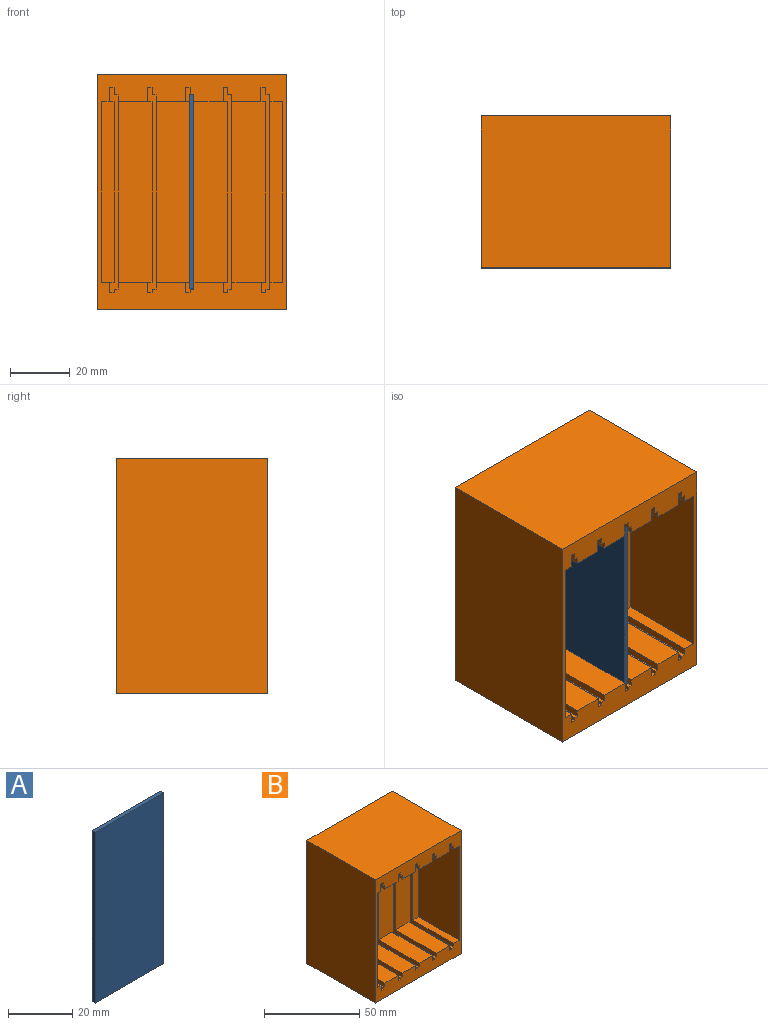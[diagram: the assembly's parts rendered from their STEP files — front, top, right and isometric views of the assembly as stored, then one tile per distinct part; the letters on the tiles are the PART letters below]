
ASSEMBLY  parts=2 mates=1
PART A: 6 faces, bbox 30.1x1.3x65 mm
  f0: plane 64.99x1.33mm, normal (1,0,0), area 86.7mm2, adj f1,f3,f4,f5
  f1: plane 30.14x1.33mm, normal (0,0,1), area 40.2mm2, adj f0,f2,f4,f5
  f2: plane 64.99x1.33mm, normal (-1,0,0), area 86.7mm2, adj f1,f3,f4,f5
  f3: plane 30.14x1.33mm, normal (0,0,-1), area 40.2mm2, adj f0,f2,f4,f5
  f4: plane 64.99x30.14mm, normal (0,-1,0), area 1958.5mm2, adj f0,f1,f2,f3
  f5: plane 64.99x30.14mm, normal (0,1,0), area 1958.5mm2, adj f0,f1,f2,f3
PART B: 91 faces, bbox 63.5x50.8x79 mm
  f0: plane 30.14x2.64mm, normal (0,0,-1), area 79.6mm2, adj f37,f38,f63,f85
  f1: plane 30.14x9.72mm, normal (0,0,-1), area 292.8mm2, adj f31,f42,f63,f81
  f2: plane 30.14x9.72mm, normal (0,0,-1), area 292.8mm2, adj f25,f46,f63,f77
  f3: plane 30.14x9.72mm, normal (0,0,-1), area 292.8mm2, adj f19,f50,f63,f73
  f4: plane 30.14x9.72mm, normal (0,0,-1), area 292.8mm2, adj f13,f54,f63,f69
  f5: plane 60.39x30.14mm, normal (-1,0,0), area 1819.9mm2, adj f6,f62,f63,f65
  f6: plane 30.14x4.29mm, normal (0,0,1), area 129.4mm2, adj f5,f7,f63,f65
  f7: plane 64.99x32.44mm, normal (-1,0,0), area 287.9mm2, adj f6,f8,f57,f62,f63,f65,f86
  f8: plane 32.44x1.33mm, normal (0,0,1), area 43.3mm2, adj f7,f9,f63,f86
  f9: plane 32.44x1.05mm, normal (-1,0,0), area 34.2mm2, adj f8,f10,f63,f86
  f10: plane 32.44x1.45mm, normal (0,0,1), area 47mm2, adj f9,f11,f63,f86
  f11: plane 32.44x3.35mm, normal (1,0,0), area 108.8mm2, adj f10,f12,f63,f66,f86
  f12: plane 30.14x9.92mm, normal (0,0,1), area 298.9mm2, adj f11,f13,f63,f69
  f13: plane 64.99x32.44mm, normal (-1,0,0), area 287.9mm2, adj f4,f12,f14,f53,f63,f69,f87
  f14: plane 32.44x1.33mm, normal (0,0,1), area 43.3mm2, adj f13,f15,f63,f87
  f15: plane 32.44x1.05mm, normal (-1,0,0), area 34.2mm2, adj f14,f16,f63,f87
  f16: plane 32.44x1.45mm, normal (0,0,1), area 47mm2, adj f15,f17,f63,f87
  f17: plane 32.44x3.35mm, normal (1,0,0), area 108.8mm2, adj f16,f18,f63,f70,f87
  f18: plane 30.14x9.92mm, normal (0,0,1), area 298.9mm2, adj f17,f19,f63,f73
  f19: plane 64.99x32.44mm, normal (-1,0,0), area 287.9mm2, adj f3,f18,f20,f49,f63,f73,f88
  f20: plane 32.44x1.33mm, normal (0,0,1), area 43.3mm2, adj f19,f21,f63,f88
  f21: plane 32.44x1.05mm, normal (-1,0,0), area 34.2mm2, adj f20,f22,f63,f88
  f22: plane 32.44x1.45mm, normal (0,0,1), area 47mm2, adj f21,f23,f63,f88
  f23: plane 32.44x3.35mm, normal (1,0,0), area 108.8mm2, adj f22,f24,f63,f74,f88
  f24: plane 30.14x9.92mm, normal (0,0,1), area 298.9mm2, adj f23,f25,f63,f77
  f25: plane 64.99x32.44mm, normal (-1,0,0), area 287.9mm2, adj f2,f24,f26,f45,f63,f77,f89
  f26: plane 32.44x1.33mm, normal (0,0,1), area 43.3mm2, adj f25,f27,f63,f89
  f27: plane 32.44x1.05mm, normal (-1,0,0), area 34.2mm2, adj f26,f28,f63,f89
  f28: plane 32.44x1.45mm, normal (0,0,1), area 47mm2, adj f27,f29,f63,f89
  f29: plane 32.44x3.35mm, normal (1,0,0), area 108.8mm2, adj f28,f30,f63,f78,f89
  f30: plane 30.14x9.92mm, normal (0,0,1), area 298.9mm2, adj f29,f31,f63,f81
  f31: plane 64.99x32.44mm, normal (-1,0,0), area 287.9mm2, adj f1,f30,f32,f41,f63,f81,f90
  f32: plane 32.44x1.33mm, normal (0,0,1), area 43.3mm2, adj f31,f33,f63,f90
  f33: plane 32.44x1.05mm, normal (-1,0,0), area 34.2mm2, adj f32,f34,f63,f90
  f34: plane 32.44x1.45mm, normal (0,0,1), area 47mm2, adj f33,f35,f63,f90
  f35: plane 32.44x3.35mm, normal (1,0,0), area 108.8mm2, adj f34,f36,f63,f82,f90
  f36: plane 30.14x2.85mm, normal (0,0,1), area 85.7mm2, adj f35,f37,f63,f85
  f37: plane 60.39x30.14mm, normal (1,0,0), area 1819.9mm2, adj f0,f36,f63,f85
  f38: plane 32.44x4.71mm, normal (1,0,0), area 152.8mm2, adj f0,f39,f63,f84,f90
  f39: plane 32.44x1.65mm, normal (0,0,-1), area 53.6mm2, adj f38,f40,f63,f90
  f40: plane 32.44x2.41mm, normal (-1,0,0), area 78.3mm2, adj f39,f41,f63,f90
  f41: plane 32.44x1.33mm, normal (0,0,-1), area 43.3mm2, adj f31,f40,f63,f90
  f42: plane 32.44x4.71mm, normal (1,0,0), area 152.8mm2, adj f1,f43,f63,f80,f89
  f43: plane 32.44x1.65mm, normal (0,0,-1), area 53.6mm2, adj f42,f44,f63,f89
  f44: plane 32.44x2.41mm, normal (-1,0,0), area 78.3mm2, adj f43,f45,f63,f89
  f45: plane 32.44x1.33mm, normal (0,0,-1), area 43.3mm2, adj f25,f44,f63,f89
  f46: plane 32.44x4.71mm, normal (1,0,0), area 152.8mm2, adj f2,f47,f63,f76,f88
  f47: plane 32.44x1.65mm, normal (0,0,-1), area 53.6mm2, adj f46,f48,f63,f88
  f48: plane 32.44x2.41mm, normal (-1,0,0), area 78.3mm2, adj f47,f49,f63,f88
  f49: plane 32.44x1.33mm, normal (0,0,-1), area 43.3mm2, adj f19,f48,f63,f88
  f50: plane 32.44x4.71mm, normal (1,0,0), area 152.8mm2, adj f3,f51,f63,f72,f87
  f51: plane 32.44x1.61mm, normal (0,0,-1), area 52.3mm2, adj f50,f52,f63,f87
  f52: plane 32.44x2.41mm, normal (-1,0,0), area 78.3mm2, adj f51,f53,f63,f87
  f53: plane 32.44x1.37mm, normal (0,0,-1), area 44.5mm2, adj f13,f52,f63,f87
  f54: plane 32.44x4.71mm, normal (1,0,0), area 152.8mm2, adj f4,f55,f63,f68,f86
  f55: plane 32.44x1.65mm, normal (0,0,-1), area 53.6mm2, adj f54,f56,f63,f86
  f56: plane 32.44x2.41mm, normal (-1,0,0), area 78.3mm2, adj f55,f57,f63,f86
  f57: plane 32.44x1.33mm, normal (0,0,-1), area 43.3mm2, adj f7,f56,f63,f86
  f58: plane 63.5x50.8mm, normal (0,0,-1), area 3225.8mm2, adj f59,f61,f63,f64
  f59: plane 78.99x50.8mm, normal (1,0,0), area 4012.9mm2, adj f58,f60,f63,f64
  f60: plane 63.5x50.8mm, normal (0,0,1), area 3225.8mm2, adj f59,f61,f63,f64
  f61: plane 78.99x50.8mm, normal (-1,0,0), area 4012.9mm2, adj f58,f60,f63,f64
  f62: plane 30.14x4.29mm, normal (0,0,-1), area 129.4mm2, adj f5,f7,f63,f65
  f63: plane 78.99x63.5mm, normal (0,-1,0), area 1255.7mm2, adj f0,f1,f2,f3,f4,f5,f6,f7
  f64: plane 78.99x63.5mm, normal (0,1,0), area 5016.1mm2, adj f58,f59,f60,f61
  f65: plane 60.39x4.29mm, normal (0,-1,0), area 259.2mm2, adj f5,f6,f7,f62
  f66: plane 2.3x1.45mm, normal (0,0,-1), area 3.3mm2, adj f11,f67,f69,f86
  f67: plane 60.39x2.3mm, normal (1,0,0), area 138.8mm2, adj f66,f68,f69,f86
  f68: plane 2.3x1.65mm, normal (0,0,1), area 3.8mm2, adj f54,f67,f69,f86
  f69: plane 60.39x11.37mm, normal (0,-1,0), area 686.4mm2, adj f4,f12,f13,f66,f67,f68
  f70: plane 2.3x1.45mm, normal (0,0,-1), area 3.3mm2, adj f17,f71,f73,f87
  f71: plane 60.39x2.3mm, normal (1,0,0), area 138.8mm2, adj f70,f72,f73,f87
  f72: plane 2.3x1.65mm, normal (0,0,1), area 3.8mm2, adj f50,f71,f73,f87
  f73: plane 60.39x11.37mm, normal (0,-1,0), area 686.4mm2, adj f3,f18,f19,f70,f71,f72
  f74: plane 2.3x1.45mm, normal (0,0,-1), area 3.3mm2, adj f23,f75,f77,f88
  f75: plane 60.39x2.3mm, normal (1,0,0), area 138.8mm2, adj f74,f76,f77,f88
  f76: plane 2.3x1.65mm, normal (0,0,1), area 3.8mm2, adj f46,f75,f77,f88
  f77: plane 60.39x11.37mm, normal (0,-1,0), area 686.4mm2, adj f2,f24,f25,f74,f75,f76
  f78: plane 2.3x1.45mm, normal (0,0,-1), area 3.3mm2, adj f29,f79,f81,f89
  f79: plane 60.39x2.3mm, normal (1,0,0), area 138.8mm2, adj f78,f80,f81,f89
  f80: plane 2.3x1.65mm, normal (0,0,1), area 3.8mm2, adj f42,f79,f81,f89
  f81: plane 60.39x11.37mm, normal (0,-1,0), area 686.4mm2, adj f1,f30,f31,f78,f79,f80
  f82: plane 2.3x1.45mm, normal (0,0,-1), area 3.3mm2, adj f35,f83,f85,f90
  f83: plane 60.39x2.3mm, normal (1,0,0), area 138.8mm2, adj f82,f84,f85,f90
  f84: plane 2.3x1.65mm, normal (0,0,1), area 3.8mm2, adj f38,f83,f85,f90
  f85: plane 60.39x4.29mm, normal (0,-1,0), area 259.2mm2, adj f0,f36,f37,f82,f83,f84
  f86: plane 68.45x2.98mm, normal (0,-1,0), area 99.3mm2, adj f7,f8,f9,f10,f11,f54,f55,f56
  f87: plane 68.45x2.98mm, normal (0,-1,0), area 99.2mm2, adj f13,f14,f15,f16,f17,f50,f51,f52
  f88: plane 68.45x2.98mm, normal (0,-1,0), area 99.3mm2, adj f19,f20,f21,f22,f23,f46,f47,f48
  f89: plane 68.45x2.98mm, normal (0,-1,0), area 99.3mm2, adj f25,f26,f27,f28,f29,f42,f43,f44
  f90: plane 68.45x2.98mm, normal (0,-1,0), area 99.3mm2, adj f31,f32,f33,f34,f35,f38,f39,f40
PLACE A rot(axis=(0,0,-1),90deg) t=(13.32,58.07,32.36)mm
PLACE B t=(13.94,21.2,32.33)mm fixed
MATE slider A.f2 <-> B.f88  axis (0,1,0) through (12.65,2.08,32.36)mm
